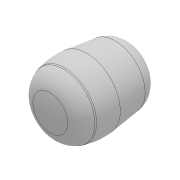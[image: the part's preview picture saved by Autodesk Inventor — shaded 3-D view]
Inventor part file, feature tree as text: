
AUTODESK INVENTOR PART (.ipt)
format: ipt  version: 2017 (Build 210142000, 142)  size: 132,608 bytes
history: native  units: mm
features: fillet x3, revolve x1, chamfer x1, sketch x1
ambient origin geometry x8: Origin, YZ Plane, XZ Plane, XY Plane, X Axis, Y Axis, Z Axis, Center Point
bodies: Solid1 (feature_tree)
feature tree (6):
  revolve  "Revolution1"  [1 undecoded]
  fillet  "Fillet1"  Radius=30.0mm
  chamfer  "Chamfer1"  Angle=90.0deg  [1 undecoded]
  fillet  "Fillet2"  Radius=20.0mm
  fillet  "Fillet3"  Radius=10.0mm
  sketch  "Sketch1"  dims[d0=40.0mm d1=80.0mm d2=30.0mm d3=90.0deg d4=20.0mm d5=10.0mm d6=20.0mm d7=45.0deg d8=20.0mm d9=60.0mm]
note: 2 required parameter values undecoded (feature->parameter linkage not recoverable at this tier; creation-order binding heuristic only, values carry confidence <= 0.55)